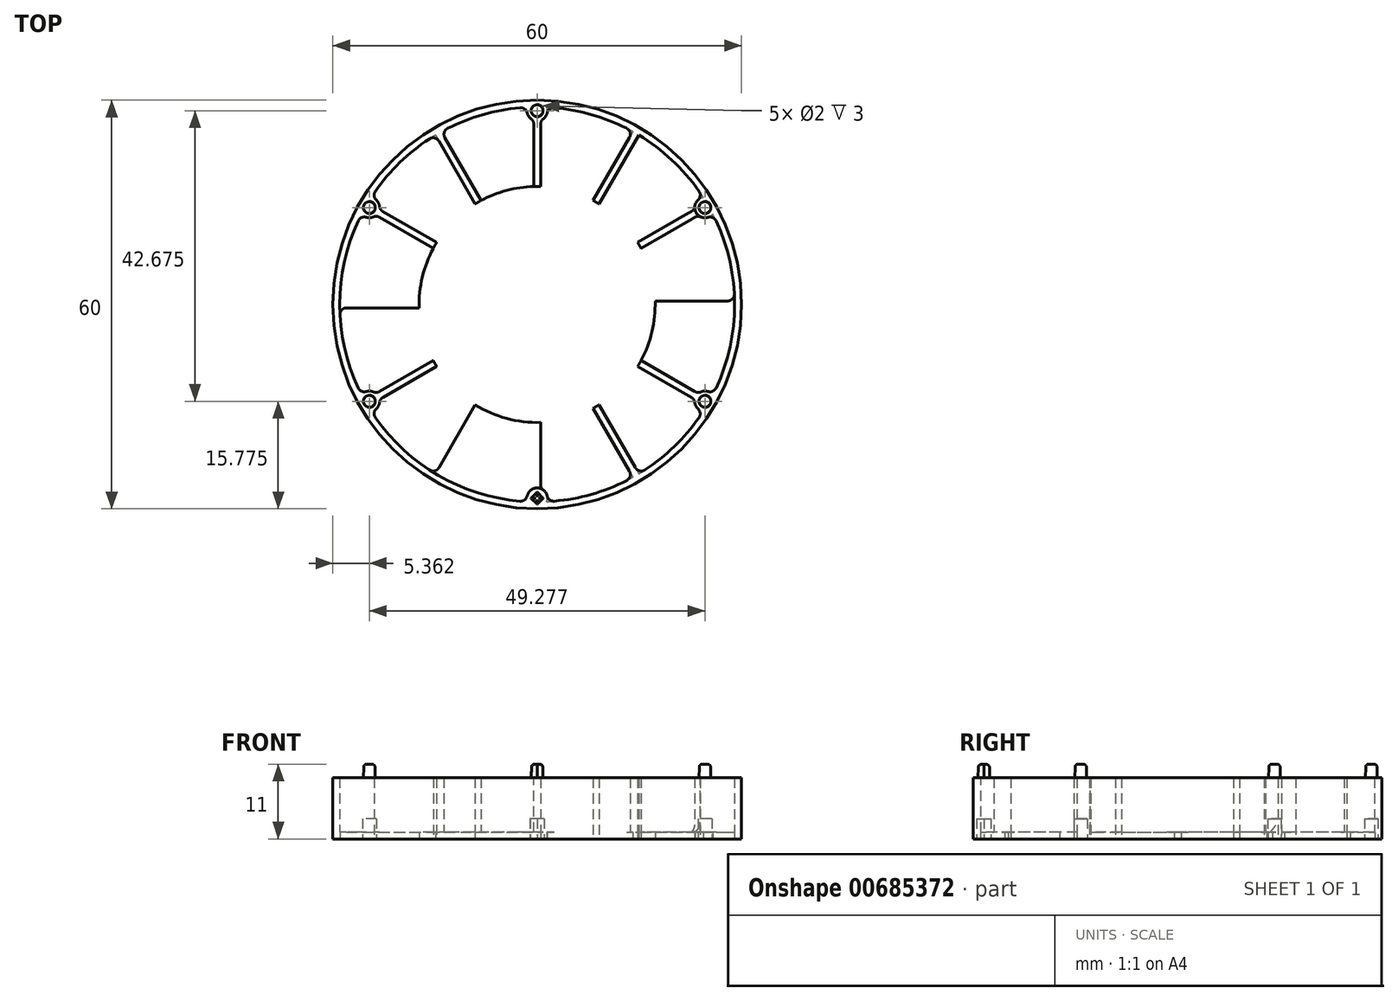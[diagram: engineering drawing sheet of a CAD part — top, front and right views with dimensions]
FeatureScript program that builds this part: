
annotation { "Feature Type Name" : "Feature", "Feature Type Description" : "" }
export const myFeature = defineFeature(function(context is Context, id is Id, definition is map)
    precondition{}
    {
        {
            var Q0;
            Q0=qCreatedBy(makeId("Top.planeOp"),FACE);
            var sketch = newSketch(context, id + "F0", { "sketchPlane" : qUnion([Q0])});
            skCircle(sketch, "E0", {"center": v(0, 0) * mm, "radius": 30 * mm});
            skCircle(sketch, "E1.0", {"center": v(0, 0) * mm, "radius": 29 * mm});
            skLineSegment(sketch, "E2.bottom", {"start": v(14.56, 26.23) * mm, "end": v(15.43, 25.73) * mm});
            skLineSegment(sketch, "E2.top", {"start": v(-15.43, -25.73) * mm, "end": v(-14.56, -26.23) * mm});
            skLineSegment(sketch, "E2.left", {"start": v(14.56, 26.23) * mm, "end": v(-15.43, -25.73) * mm});
            skLineSegment(sketch, "E2.right", {"start": v(15.43, 25.73) * mm, "end": v(-14.56, -26.23) * mm});
            skLineSegment(sketch, "E3.bottom", {"start": v(25.73, 15.43) * mm, "end": v(26.23, 14.56) * mm});
            skLineSegment(sketch, "E3.top", {"start": v(-26.23, -14.56) * mm, "end": v(-25.73, -15.43) * mm});
            skLineSegment(sketch, "E3.left", {"start": v(25.73, 15.43) * mm, "end": v(-26.23, -14.56) * mm});
            skLineSegment(sketch, "E3.right", {"start": v(26.23, 14.56) * mm, "end": v(-25.73, -15.43) * mm});
            skLineSegment(sketch, "E4", {"start": v(-38.35, 0) * mm, "end": v(39.17, 0) * mm, "construction": true});
            skLineSegment(sketch, "E5", {"start": v(0, 42.5) * mm, "end": v(0, -42.47) * mm, "construction": true});
            skLineSegment(sketch, "E6.bottom", {"start": v(-30, 0.5) * mm, "end": v(30, 0.5) * mm});
            skLineSegment(sketch, "E6.top", {"start": v(-30, -0.5) * mm, "end": v(30, -0.5) * mm});
            skLineSegment(sketch, "E6.left", {"start": v(-30, 0.5) * mm, "end": v(-30, -0.5) * mm});
            skLineSegment(sketch, "E6.right", {"start": v(30, 0.5) * mm, "end": v(30, -0.5) * mm});
            skLineSegment(sketch, "E7.bottom", {"start": v(-25.73, 15.43) * mm, "end": v(26.23, -14.56) * mm});
            skLineSegment(sketch, "E7.top", {"start": v(-26.23, 14.56) * mm, "end": v(25.73, -15.43) * mm});
            skLineSegment(sketch, "E7.left", {"start": v(-25.73, 15.43) * mm, "end": v(-26.23, 14.56) * mm});
            skLineSegment(sketch, "E7.right", {"start": v(26.23, -14.56) * mm, "end": v(25.73, -15.43) * mm});
            skLineSegment(sketch, "E8.bottom", {"start": v(-0.5, 30) * mm, "end": v(0.5, 30) * mm});
            skLineSegment(sketch, "E8.top", {"start": v(-0.5, -30) * mm, "end": v(0.5, -30) * mm});
            skLineSegment(sketch, "E8.left", {"start": v(-0.5, 30) * mm, "end": v(-0.5, -30) * mm});
            skLineSegment(sketch, "E8.right", {"start": v(0.5, 30) * mm, "end": v(0.5, -30) * mm});
            skLineSegment(sketch, "E9.bottom", {"start": v(-15.43, 25.73) * mm, "end": v(-14.56, 26.23) * mm});
            skLineSegment(sketch, "E9.top", {"start": v(14.56, -26.23) * mm, "end": v(15.43, -25.73) * mm});
            skLineSegment(sketch, "E9.left", {"start": v(-15.43, 25.73) * mm, "end": v(14.56, -26.23) * mm});
            skLineSegment(sketch, "E9.right", {"start": v(-14.56, 26.23) * mm, "end": v(15.43, -25.73) * mm});
            skCircle(sketch, "E10", {"center": v(0, 0) * mm, "radius": 17.33 * mm});
            skSolve(sketch);
        }
        {
            var Q0;
            Q0=qCreatedBy(makeId("Top.planeOp"),FACE);
            var sketch = newSketch(context, id + "F1", { "sketchPlane" : qUnion([Q0])});
            skCircle(sketch, "E11", {"center": v(0, 0) * mm, "radius": 30 * mm});
            skCircle(sketch, "E12", {"center": v(0, 0) * mm, "radius": 29 * mm});
            skSolve(sketch);
        }
        {
            var Q0;
            Q0=makeQuery(id+"F1.imprint","IMPRINT",FACE,{"disambiguationData":[TD([[makeQuery(id+"F1.imprint","IMPRINT",EDGE,{"derivedFrom":sQuery(id+"F1.wireOp",EDGE,"E11")}),1.0]])]});
            extrude(context, id + "F2", {"entities" : qUnion([Q0]), "depth" : 9 * mm, "offsetDistance" : 25 * mm});
        }
        {
            var Q0;
            {var subQ0=sQuery(id+"F0.wireOp",EDGE,"E7.bottom");var subQ1=sQuery(id+"F0.wireOp",EDGE,"E1.0");var subQ2=makeQuery(id+"F0.imprint","INTERSECT",VERTEX,{"disambiguationData":[OD(0.0)],"derivedFrom":[subQ1,subQ0]});Q0=makeQuery(id+"F0.imprint","IMPRINT",FACE,{"disambiguationData":[TD([[makeQuery(id+"F0.imprint","IMPRINT",EDGE,{"disambiguationData":[TD([[subQ2,-1.0]])],"derivedFrom":subQ1}),1.0]])]});}
            var Q1;
            {var subQ0=sQuery(id+"F0.wireOp",EDGE,"E2.right");var subQ1=sQuery(id+"F0.wireOp",EDGE,"E1.0");var subQ2=makeQuery(id+"F0.imprint","INTERSECT",VERTEX,{"disambiguationData":[OD(0.0)],"derivedFrom":[subQ1,subQ0]});Q1=makeQuery(id+"F0.imprint","IMPRINT",FACE,{"disambiguationData":[TD([[makeQuery(id+"F0.imprint","IMPRINT",EDGE,{"disambiguationData":[TD([[subQ2,-1.0]])],"derivedFrom":subQ1}),1.0]])]});}
            var Q2;
            {var subQ0=sQuery(id+"F0.wireOp",EDGE,"E3.left");var subQ1=sQuery(id+"F0.wireOp",EDGE,"E1.0");var subQ2=makeQuery(id+"F0.imprint","INTERSECT",VERTEX,{"disambiguationData":[OD(1.0)],"derivedFrom":[subQ1,subQ0]});Q2=makeQuery(id+"F0.imprint","IMPRINT",FACE,{"disambiguationData":[TD([[makeQuery(id+"F0.imprint","IMPRINT",EDGE,{"disambiguationData":[TD([[subQ2,-1.0]])],"derivedFrom":subQ1}),1.0]])]});}
            var Q3;
            {var subQ0=sQuery(id+"F0.wireOp",EDGE,"E9.right");var subQ1=sQuery(id+"F0.wireOp",EDGE,"E1.0");var subQ2=makeQuery(id+"F0.imprint","INTERSECT",VERTEX,{"disambiguationData":[OD(0.0)],"derivedFrom":[subQ1,subQ0]});Q3=makeQuery(id+"F0.imprint","IMPRINT",FACE,{"disambiguationData":[TD([[makeQuery(id+"F0.imprint","IMPRINT",EDGE,{"disambiguationData":[TD([[subQ2,-1.0]])],"derivedFrom":subQ1}),1.0]])]});}
            var Q4;
            {var subQ0=sQuery(id+"F0.wireOp",EDGE,"E8.right");var subQ1=sQuery(id+"F0.wireOp",EDGE,"E1.0");var subQ2=makeQuery(id+"F0.imprint","INTERSECT",VERTEX,{"disambiguationData":[OD(0.0)],"derivedFrom":[subQ1,subQ0]});Q4=makeQuery(id+"F0.imprint","IMPRINT",FACE,{"disambiguationData":[TD([[makeQuery(id+"F0.imprint","IMPRINT",EDGE,{"disambiguationData":[TD([[subQ2,-1.0]])],"derivedFrom":subQ1}),1.0]])]});}
            var Q5;
            {var subQ0=sQuery(id+"F0.wireOp",EDGE,"E7.top");var subQ1=sQuery(id+"F0.wireOp",EDGE,"E1.0");var subQ2=makeQuery(id+"F0.imprint","INTERSECT",VERTEX,{"disambiguationData":[OD(1.0)],"derivedFrom":[subQ1,subQ0]});Q5=makeQuery(id+"F0.imprint","IMPRINT",FACE,{"disambiguationData":[TD([[makeQuery(id+"F0.imprint","IMPRINT",EDGE,{"disambiguationData":[TD([[subQ2,-1.0]])],"derivedFrom":subQ1}),1.0]])]});}
            var Q6;
            {var subQ0=sQuery(id+"F0.wireOp",EDGE,"E9.left");var subQ1=sQuery(id+"F0.wireOp",EDGE,"E1.0");var subQ2=makeQuery(id+"F0.imprint","INTERSECT",VERTEX,{"disambiguationData":[OD(1.0)],"derivedFrom":[subQ1,subQ0]});Q6=makeQuery(id+"F0.imprint","IMPRINT",FACE,{"disambiguationData":[TD([[makeQuery(id+"F0.imprint","IMPRINT",EDGE,{"disambiguationData":[TD([[subQ2,-1.0]])],"derivedFrom":subQ1}),1.0]])]});}
            extrude(context, id + "F3", {"entities" : qUnion([Q0, Q1, Q2, Q3, Q4, Q5, Q6]), "operationType" : NewBodyOperationType.ADD, "depth" : 9 * mm, "offsetDistance" : 25 * mm});
        }
        {
            var Q0;
            Q0=makeQuery(id+"F1.imprint","IMPRINT",FACE,{"disambiguationData":[TD([[makeQuery(id+"F1.imprint","IMPRINT",EDGE,{"derivedFrom":sQuery(id+"F1.wireOp",EDGE,"E11")}),1.0]])]});
            var Q1;
            Q1=makeQuery(id+"F1.imprint","IMPRINT",FACE,{"disambiguationData":[TD([[makeQuery(id+"F1.imprint","IMPRINT",EDGE,{"derivedFrom":sQuery(id+"F1.wireOp",EDGE,"E12")}),1.0]])]});
            extrude(context, id + "F4", {"entities" : qUnion([Q0, Q1]), "operationType" : NewBodyOperationType.ADD, "depth" : 1 * mm, "offsetDistance" : 25 * mm});
        }
        {
            var Q0;
            {var subQ0=sQuery(id+"F0.wireOp",EDGE,"E8.right");var subQ1=sQuery(id+"F0.wireOp",EDGE,"E1.0");var subQ2=makeQuery(id+"F0.imprint","INTERSECT",VERTEX,{"disambiguationData":[OD(1.0)],"derivedFrom":[subQ1,subQ0]});Q0=makeQuery(id+"F0.imprint","IMPRINT",FACE,{"disambiguationData":[TD([[makeQuery(id+"F0.imprint","IMPRINT",EDGE,{"disambiguationData":[TD([[subQ2,-1.0]])],"derivedFrom":subQ1}),1.0]])]});}
            var Q1;
            {var subQ0=sQuery(id+"F0.wireOp",EDGE,"E9.right");var subQ1=sQuery(id+"F0.wireOp",EDGE,"E1.0");var subQ2=makeQuery(id+"F0.imprint","INTERSECT",VERTEX,{"disambiguationData":[OD(1.0)],"derivedFrom":[subQ1,subQ0]});Q1=makeQuery(id+"F0.imprint","IMPRINT",FACE,{"disambiguationData":[TD([[makeQuery(id+"F0.imprint","IMPRINT",EDGE,{"disambiguationData":[TD([[subQ2,-1.0]])],"derivedFrom":subQ1}),1.0]])]});}
            var Q2;
            {var subQ0=sQuery(id+"F0.wireOp",EDGE,"E3.right");var subQ1=sQuery(id+"F0.wireOp",EDGE,"E1.0");var subQ2=makeQuery(id+"F0.imprint","INTERSECT",VERTEX,{"disambiguationData":[OD(0.0)],"derivedFrom":[subQ1,subQ0]});Q2=makeQuery(id+"F0.imprint","IMPRINT",FACE,{"disambiguationData":[TD([[makeQuery(id+"F0.imprint","IMPRINT",EDGE,{"disambiguationData":[TD([[subQ2,1.0]])],"derivedFrom":subQ1}),1.0]])]});}
            var Q3;
            {var subQ0=sQuery(id+"F0.wireOp",EDGE,"E3.left");var subQ1=sQuery(id+"F0.wireOp",EDGE,"E1.0");var subQ2=makeQuery(id+"F0.imprint","INTERSECT",VERTEX,{"disambiguationData":[OD(0.0)],"derivedFrom":[subQ1,subQ0]});Q3=makeQuery(id+"F0.imprint","IMPRINT",FACE,{"disambiguationData":[TD([[makeQuery(id+"F0.imprint","IMPRINT",EDGE,{"disambiguationData":[TD([[subQ2,-1.0]])],"derivedFrom":subQ1}),1.0]])]});}
            var Q4;
            {var subQ0=sQuery(id+"F0.wireOp",EDGE,"E2.left");var subQ1=sQuery(id+"F0.wireOp",EDGE,"E1.0");var subQ2=makeQuery(id+"F0.imprint","INTERSECT",VERTEX,{"disambiguationData":[OD(0.0)],"derivedFrom":[subQ1,subQ0]});Q4=makeQuery(id+"F0.imprint","IMPRINT",FACE,{"disambiguationData":[TD([[makeQuery(id+"F0.imprint","IMPRINT",EDGE,{"disambiguationData":[TD([[subQ2,-1.0]])],"derivedFrom":subQ1}),1.0]])]});}
            var Q5;
            {var subQ0=sQuery(id+"F0.wireOp",EDGE,"E9.left");var subQ1=sQuery(id+"F0.wireOp",EDGE,"E1.0");var subQ2=makeQuery(id+"F0.imprint","INTERSECT",VERTEX,{"disambiguationData":[OD(0.0)],"derivedFrom":[subQ1,subQ0]});Q5=makeQuery(id+"F0.imprint","IMPRINT",FACE,{"disambiguationData":[TD([[makeQuery(id+"F0.imprint","IMPRINT",EDGE,{"disambiguationData":[TD([[subQ2,-1.0]])],"derivedFrom":subQ1}),1.0]])]});}
            var Q6;
            {var subQ0=sQuery(id+"F0.wireOp",EDGE,"E6.top");var subQ1=sQuery(id+"F0.wireOp",EDGE,"E1.0");var subQ2=makeQuery(id+"F0.imprint","INTERSECT",VERTEX,{"disambiguationData":[OD(0.0)],"derivedFrom":[subQ1,subQ0]});Q6=makeQuery(id+"F0.imprint","IMPRINT",FACE,{"disambiguationData":[TD([[makeQuery(id+"F0.imprint","IMPRINT",EDGE,{"disambiguationData":[TD([[subQ2,-1.0]])],"derivedFrom":subQ1}),1.0]])]});}
            var Q7;
            {var subQ0=sQuery(id+"F0.wireOp",EDGE,"E3.right");var subQ1=sQuery(id+"F0.wireOp",EDGE,"E1.0");var subQ2=makeQuery(id+"F0.imprint","INTERSECT",VERTEX,{"disambiguationData":[OD(1.0)],"derivedFrom":[subQ1,subQ0]});Q7=makeQuery(id+"F0.imprint","IMPRINT",FACE,{"disambiguationData":[TD([[makeQuery(id+"F0.imprint","IMPRINT",EDGE,{"disambiguationData":[TD([[subQ2,-1.0]])],"derivedFrom":subQ1}),1.0]])]});}
            extrude(context, id + "F5", {"entities" : qUnion([Q0, Q1, Q2, Q3, Q4, Q5, Q6, Q7]), "operationType" : NewBodyOperationType.REMOVE, "depth" : 1 * mm, "offsetDistance" : 25 * mm});
        }
        {
            var Q0;
            Q0=qCreatedBy(makeId("Top.planeOp"),FACE);
            var sketch = newSketch(context, id + "F6", { "sketchPlane" : qUnion([Q0])});
            skCircle(sketch, "E13", {"center": v(0, 0) * mm, "radius": 28.45 * mm});
            skLineSegment(sketch, "E14", {"start": v(0, 28.45) * mm, "end": v(0, -28.45) * mm, "construction": true});
            skLineSegment(sketch, "E15", {"start": v(24.64, 14.22) * mm, "end": v(0, 0) * mm, "construction": true});
            skLineSegment(sketch, "E16", {"start": v(14.23, 24.64) * mm, "end": v(0, 0) * mm, "construction": true});
            skLineSegment(sketch, "E17", {"start": v(0, 0) * mm, "end": v(28.45, 0) * mm, "construction": true});
            skLineSegment(sketch, "E18", {"start": v(0, 0) * mm, "end": v(24.64, -14.22) * mm, "construction": true});
            skLineSegment(sketch, "E19", {"start": v(0, 0) * mm, "end": v(14.23, -24.64) * mm, "construction": true});
            skLineSegment(sketch, "E20", {"start": v(0, 0) * mm, "end": v(-14.23, 24.64) * mm, "construction": true});
            skLineSegment(sketch, "E21", {"start": v(0, 0) * mm, "end": v(-24.64, 14.22) * mm, "construction": true});
            skLineSegment(sketch, "E22", {"start": v(0, 0) * mm, "end": v(-28.45, 0) * mm, "construction": true});
            skLineSegment(sketch, "E23", {"start": v(0, 0) * mm, "end": v(-24.64, -14.23) * mm, "construction": true});
            skLineSegment(sketch, "E24", {"start": v(0, 0) * mm, "end": v(-14.22, -24.64) * mm, "construction": true});
            skCircle(sketch, "E25", {"center": v(0, 28.45) * mm, "radius": 1.5 * mm});
            skCircle(sketch, "E26", {"center": v(24.64, 14.22) * mm, "radius": 1.5 * mm});
            skCircle(sketch, "E27", {"center": v(24.64, -14.22) * mm, "radius": 1.5 * mm});
            skCircle(sketch, "E28", {"center": v(0, -28.45) * mm, "radius": 1.5 * mm});
            skCircle(sketch, "E29", {"center": v(-24.64, -14.23) * mm, "radius": 1.5 * mm});
            skCircle(sketch, "E30", {"center": v(-24.64, 14.22) * mm, "radius": 1.5 * mm});
            skCircle(sketch, "E31", {"center": v(-24.64, 14.22) * mm, "radius": 1 * mm});
            skCircle(sketch, "E32", {"center": v(0, 28.45) * mm, "radius": 1 * mm});
            skCircle(sketch, "E33", {"center": v(24.64, 14.22) * mm, "radius": 1 * mm});
            skCircle(sketch, "E34", {"center": v(24.64, -14.22) * mm, "radius": 1 * mm});
            skCircle(sketch, "E35", {"center": v(-24.64, -14.23) * mm, "radius": 1 * mm});
            skLineSegment(sketch, "E36.bottom", {"start": v(1.06, -28.45) * mm, "end": v(0, -29.51) * mm});
            skLineSegment(sketch, "E36.top", {"start": v(0, -27.39) * mm, "end": v(-1.06, -28.45) * mm});
            skLineSegment(sketch, "E36.left", {"start": v(1.06, -28.45) * mm, "end": v(0, -27.39) * mm});
            skLineSegment(sketch, "E36.right", {"start": v(0, -29.51) * mm, "end": v(-1.06, -28.45) * mm});
            skSolve(sketch);
        }
        {
            var Q0;
            {var subQ0=sQuery(id+"F6.wireOp",EDGE,"E30");var subQ1=sQuery(id+"F6.wireOp",EDGE,"E13");var subQ2=makeQuery(id+"F6.imprint","INTERSECT",VERTEX,{"disambiguationData":[OD(0.0)],"derivedFrom":[subQ1,subQ0]});Q0=makeQuery(id+"F6.imprint","IMPRINT",FACE,{"disambiguationData":[TD([[makeQuery(id+"F6.imprint","IMPRINT",EDGE,{"disambiguationData":[TD([[subQ2,-1.0]])],"derivedFrom":subQ1}),1.0]])]});}
            var Q1;
            {var subQ0=sQuery(id+"F6.wireOp",EDGE,"E30");var subQ1=sQuery(id+"F6.wireOp",EDGE,"E13");var subQ2=makeQuery(id+"F6.imprint","INTERSECT",VERTEX,{"disambiguationData":[OD(0.0)],"derivedFrom":[subQ1,subQ0]});Q1=makeQuery(id+"F6.imprint","IMPRINT",FACE,{"disambiguationData":[TD([[makeQuery(id+"F6.imprint","IMPRINT",EDGE,{"disambiguationData":[TD([[subQ2,-1.0]])],"derivedFrom":subQ1}),-1.0]])]});}
            var Q2;
            {var subQ0=sQuery(id+"F6.wireOp",EDGE,"E25");var subQ1=sQuery(id+"F6.wireOp",EDGE,"E13");var subQ2=makeQuery(id+"F6.imprint","INTERSECT",VERTEX,{"disambiguationData":[OD(0.0)],"derivedFrom":[subQ1,subQ0]});Q2=makeQuery(id+"F6.imprint","IMPRINT",FACE,{"disambiguationData":[TD([[makeQuery(id+"F6.imprint","IMPRINT",EDGE,{"disambiguationData":[TD([[subQ2,-1.0]])],"derivedFrom":subQ1}),1.0]])]});}
            var Q3;
            {var subQ0=sQuery(id+"F6.wireOp",EDGE,"E25");var subQ1=sQuery(id+"F6.wireOp",EDGE,"E13");var subQ2=makeQuery(id+"F6.imprint","INTERSECT",VERTEX,{"disambiguationData":[OD(0.0)],"derivedFrom":[subQ1,subQ0]});Q3=makeQuery(id+"F6.imprint","IMPRINT",FACE,{"disambiguationData":[TD([[makeQuery(id+"F6.imprint","IMPRINT",EDGE,{"disambiguationData":[TD([[subQ2,-1.0]])],"derivedFrom":subQ1}),-1.0]])]});}
            var Q4;
            {var subQ0=sQuery(id+"F6.wireOp",EDGE,"E26");var subQ1=sQuery(id+"F6.wireOp",EDGE,"E13");var subQ2=makeQuery(id+"F6.imprint","INTERSECT",VERTEX,{"disambiguationData":[OD(0.0)],"derivedFrom":[subQ1,subQ0]});Q4=makeQuery(id+"F6.imprint","IMPRINT",FACE,{"disambiguationData":[TD([[makeQuery(id+"F6.imprint","IMPRINT",EDGE,{"disambiguationData":[TD([[subQ2,-1.0]])],"derivedFrom":subQ1}),-1.0]])]});}
            var Q5;
            {var subQ0=sQuery(id+"F6.wireOp",EDGE,"E26");var subQ1=sQuery(id+"F6.wireOp",EDGE,"E13");var subQ2=makeQuery(id+"F6.imprint","INTERSECT",VERTEX,{"disambiguationData":[OD(0.0)],"derivedFrom":[subQ1,subQ0]});Q5=makeQuery(id+"F6.imprint","IMPRINT",FACE,{"disambiguationData":[TD([[makeQuery(id+"F6.imprint","IMPRINT",EDGE,{"disambiguationData":[TD([[subQ2,-1.0]])],"derivedFrom":subQ1}),1.0]])]});}
            var Q6;
            {var subQ0=sQuery(id+"F6.wireOp",EDGE,"E29");var subQ1=sQuery(id+"F6.wireOp",EDGE,"E13");var subQ2=makeQuery(id+"F6.imprint","INTERSECT",VERTEX,{"disambiguationData":[OD(0.0)],"derivedFrom":[subQ1,subQ0]});Q6=makeQuery(id+"F6.imprint","IMPRINT",FACE,{"disambiguationData":[TD([[makeQuery(id+"F6.imprint","IMPRINT",EDGE,{"disambiguationData":[TD([[subQ2,-1.0]])],"derivedFrom":subQ1}),1.0]])]});}
            var Q7;
            {var subQ0=sQuery(id+"F6.wireOp",EDGE,"E29");var subQ1=sQuery(id+"F6.wireOp",EDGE,"E13");var subQ2=makeQuery(id+"F6.imprint","INTERSECT",VERTEX,{"disambiguationData":[OD(0.0)],"derivedFrom":[subQ1,subQ0]});Q7=makeQuery(id+"F6.imprint","IMPRINT",FACE,{"disambiguationData":[TD([[makeQuery(id+"F6.imprint","IMPRINT",EDGE,{"disambiguationData":[TD([[subQ2,-1.0]])],"derivedFrom":subQ1}),-1.0]])]});}
            var Q8;
            {var subQ3=sQuery(id+"F6.wireOp",EDGE,"E13");var subQ5=sQuery(id+"F6.wireOp",EDGE,"E28");var subQ6=makeQuery(id+"F6.imprint","INTERSECT",VERTEX,{"disambiguationData":[OD(0.0)],"derivedFrom":[subQ3,subQ5]});Q8=makeQuery(id+"F6.imprint","IMPRINT",FACE,{"disambiguationData":[TD([[makeQuery(id+"F6.imprint","IMPRINT",EDGE,{"disambiguationData":[TD([[subQ6,-1.0]])],"derivedFrom":subQ3}),1.0]])]});}
            var Q9;
            {var subQ6=sQuery(id+"F6.wireOp",EDGE,"E36.bottom");Q9=makeQuery(id+"F6.imprint","IMPRINT",FACE,{"disambiguationData":[TD([[makeQuery(id+"F6.imprint","IMPRINT",EDGE,{"derivedFrom":subQ6}),1.0]])]});}
            var Q10;
            {var subQ0=sQuery(id+"F6.wireOp",EDGE,"E27");var subQ1=sQuery(id+"F6.wireOp",EDGE,"E13");var subQ2=makeQuery(id+"F6.imprint","INTERSECT",VERTEX,{"disambiguationData":[OD(0.0)],"derivedFrom":[subQ1,subQ0]});Q10=makeQuery(id+"F6.imprint","IMPRINT",FACE,{"disambiguationData":[TD([[makeQuery(id+"F6.imprint","IMPRINT",EDGE,{"disambiguationData":[TD([[subQ2,-1.0]])],"derivedFrom":subQ1}),-1.0]])]});}
            var Q11;
            {var subQ0=sQuery(id+"F6.wireOp",EDGE,"E27");var subQ1=sQuery(id+"F6.wireOp",EDGE,"E13");var subQ2=makeQuery(id+"F6.imprint","INTERSECT",VERTEX,{"disambiguationData":[OD(0.0)],"derivedFrom":[subQ1,subQ0]});Q11=makeQuery(id+"F6.imprint","IMPRINT",FACE,{"disambiguationData":[TD([[makeQuery(id+"F6.imprint","IMPRINT",EDGE,{"disambiguationData":[TD([[subQ2,-1.0]])],"derivedFrom":subQ1}),1.0]])]});}
            var Q12;
            {var subQ0=sQuery(id+"F6.wireOp",EDGE,"E31");var subQ1=sQuery(id+"F6.wireOp",EDGE,"E13");var subQ2=makeQuery(id+"F6.imprint","INTERSECT",VERTEX,{"disambiguationData":[OD(0.0)],"derivedFrom":[subQ1,subQ0]});Q12=makeQuery(id+"F6.imprint","IMPRINT",FACE,{"disambiguationData":[TD([[makeQuery(id+"F6.imprint","IMPRINT",EDGE,{"disambiguationData":[TD([[subQ2,-1.0]])],"derivedFrom":subQ1}),1.0]])]});}
            var Q13;
            {var subQ0=sQuery(id+"F6.wireOp",EDGE,"E31");var subQ1=sQuery(id+"F6.wireOp",EDGE,"E13");var subQ2=makeQuery(id+"F6.imprint","INTERSECT",VERTEX,{"disambiguationData":[OD(0.0)],"derivedFrom":[subQ1,subQ0]});Q13=makeQuery(id+"F6.imprint","IMPRINT",FACE,{"disambiguationData":[TD([[makeQuery(id+"F6.imprint","IMPRINT",EDGE,{"disambiguationData":[TD([[subQ2,-1.0]])],"derivedFrom":subQ1}),-1.0]])]});}
            var Q14;
            {var subQ0=sQuery(id+"F6.wireOp",EDGE,"E32");var subQ1=sQuery(id+"F6.wireOp",EDGE,"E13");var subQ2=makeQuery(id+"F6.imprint","INTERSECT",VERTEX,{"disambiguationData":[OD(0.0)],"derivedFrom":[subQ1,subQ0]});Q14=makeQuery(id+"F6.imprint","IMPRINT",FACE,{"disambiguationData":[TD([[makeQuery(id+"F6.imprint","IMPRINT",EDGE,{"disambiguationData":[TD([[subQ2,-1.0]])],"derivedFrom":subQ1}),-1.0]])]});}
            var Q15;
            {var subQ0=sQuery(id+"F6.wireOp",EDGE,"E32");var subQ1=sQuery(id+"F6.wireOp",EDGE,"E13");var subQ2=makeQuery(id+"F6.imprint","INTERSECT",VERTEX,{"disambiguationData":[OD(0.0)],"derivedFrom":[subQ1,subQ0]});Q15=makeQuery(id+"F6.imprint","IMPRINT",FACE,{"disambiguationData":[TD([[makeQuery(id+"F6.imprint","IMPRINT",EDGE,{"disambiguationData":[TD([[subQ2,-1.0]])],"derivedFrom":subQ1}),1.0]])]});}
            var Q16;
            {var subQ0=sQuery(id+"F6.wireOp",EDGE,"E33");var subQ1=sQuery(id+"F6.wireOp",EDGE,"E13");var subQ2=makeQuery(id+"F6.imprint","INTERSECT",VERTEX,{"disambiguationData":[OD(0.0)],"derivedFrom":[subQ1,subQ0]});Q16=makeQuery(id+"F6.imprint","IMPRINT",FACE,{"disambiguationData":[TD([[makeQuery(id+"F6.imprint","IMPRINT",EDGE,{"disambiguationData":[TD([[subQ2,-1.0]])],"derivedFrom":subQ1}),-1.0]])]});}
            var Q17;
            {var subQ0=sQuery(id+"F6.wireOp",EDGE,"E33");var subQ1=sQuery(id+"F6.wireOp",EDGE,"E13");var subQ2=makeQuery(id+"F6.imprint","INTERSECT",VERTEX,{"disambiguationData":[OD(0.0)],"derivedFrom":[subQ1,subQ0]});Q17=makeQuery(id+"F6.imprint","IMPRINT",FACE,{"disambiguationData":[TD([[makeQuery(id+"F6.imprint","IMPRINT",EDGE,{"disambiguationData":[TD([[subQ2,-1.0]])],"derivedFrom":subQ1}),1.0]])]});}
            var Q18;
            {var subQ0=sQuery(id+"F6.wireOp",EDGE,"E34");var subQ1=sQuery(id+"F6.wireOp",EDGE,"E13");var subQ2=makeQuery(id+"F6.imprint","INTERSECT",VERTEX,{"disambiguationData":[OD(0.0)],"derivedFrom":[subQ1,subQ0]});Q18=makeQuery(id+"F6.imprint","IMPRINT",FACE,{"disambiguationData":[TD([[makeQuery(id+"F6.imprint","IMPRINT",EDGE,{"disambiguationData":[TD([[subQ2,-1.0]])],"derivedFrom":subQ1}),-1.0]])]});}
            var Q19;
            {var subQ0=sQuery(id+"F6.wireOp",EDGE,"E34");var subQ1=sQuery(id+"F6.wireOp",EDGE,"E13");var subQ2=makeQuery(id+"F6.imprint","INTERSECT",VERTEX,{"disambiguationData":[OD(0.0)],"derivedFrom":[subQ1,subQ0]});Q19=makeQuery(id+"F6.imprint","IMPRINT",FACE,{"disambiguationData":[TD([[makeQuery(id+"F6.imprint","IMPRINT",EDGE,{"disambiguationData":[TD([[subQ2,-1.0]])],"derivedFrom":subQ1}),1.0]])]});}
            var Q20;
            {var subQ1=sQuery(id+"F6.wireOp",EDGE,"E36.bottom");Q20=makeQuery(id+"F6.imprint","IMPRINT",FACE,{"disambiguationData":[TD([[makeQuery(id+"F6.imprint","IMPRINT",EDGE,{"derivedFrom":subQ1}),-1.0]])]});}
            var Q21;
            {var subQ0=sQuery(id+"F6.wireOp",EDGE,"E35");var subQ1=sQuery(id+"F6.wireOp",EDGE,"E13");var subQ2=makeQuery(id+"F6.imprint","INTERSECT",VERTEX,{"disambiguationData":[OD(0.0)],"derivedFrom":[subQ1,subQ0]});Q21=makeQuery(id+"F6.imprint","IMPRINT",FACE,{"disambiguationData":[TD([[makeQuery(id+"F6.imprint","IMPRINT",EDGE,{"disambiguationData":[TD([[subQ2,-1.0]])],"derivedFrom":subQ1}),-1.0]])]});}
            var Q22;
            {var subQ0=sQuery(id+"F6.wireOp",EDGE,"E35");var subQ1=sQuery(id+"F6.wireOp",EDGE,"E13");var subQ2=makeQuery(id+"F6.imprint","INTERSECT",VERTEX,{"disambiguationData":[OD(0.0)],"derivedFrom":[subQ1,subQ0]});Q22=makeQuery(id+"F6.imprint","IMPRINT",FACE,{"disambiguationData":[TD([[makeQuery(id+"F6.imprint","IMPRINT",EDGE,{"disambiguationData":[TD([[subQ2,-1.0]])],"derivedFrom":subQ1}),1.0]])]});}
            var Q23;
            {var subQ0=sQuery(id+"F6.wireOp",EDGE,"E36.top");var subQ1=sQuery(id+"F6.wireOp",EDGE,"E13");var subQ2=makeQuery(id+"F6.imprint","INTERSECT",VERTEX,{"derivedFrom":[subQ1,subQ0]});Q23=makeQuery(id+"F6.imprint","IMPRINT",FACE,{"disambiguationData":[TD([[makeQuery(id+"F6.imprint","IMPRINT",EDGE,{"disambiguationData":[TD([[subQ2,-1.0]])],"derivedFrom":subQ1}),1.0]])]});}
            extrude(context, id + "F7", {"entities" : qUnion([Q0, Q1, Q2, Q3, Q4, Q5, Q6, Q7, Q8, Q9, Q10, Q11, Q12, Q13, Q14, Q15, Q16, Q17, Q18, Q19, Q20, Q21, Q22, Q23]), "operationType" : NewBodyOperationType.ADD, "depth" : 9 * mm, "offsetDistance" : 25 * mm});
        }
        {
            var Q0;
            {var subQ0=sQuery(id+"F0.wireOp",EDGE,"E8.right");var subQ1=sQuery(id+"F0.wireOp",EDGE,"E1.0");Q0=makeQuery(id+"F3.opExtrude","SWEPT_EDGE",EDGE,{"disambiguationData":[OSD([subQ1,subQ0]),TDD([makeQuery(id+"F0.imprint","INTERSECT",VERTEX,{"disambiguationData":[OD(1.0)],"derivedFrom":[subQ1,subQ0]})])]});}
            var Q1;
            {var subQ0=sQuery(id+"F0.wireOp",EDGE,"E2.left");var subQ1=sQuery(id+"F0.wireOp",EDGE,"E1.0");Q1=makeQuery(id+"F3.opExtrude","SWEPT_EDGE",EDGE,{"disambiguationData":[OSD([subQ1,subQ0]),TDD([makeQuery(id+"F0.imprint","INTERSECT",VERTEX,{"disambiguationData":[OD(1.0)],"derivedFrom":[subQ1,subQ0]})])]});}
            var Q2;
            {var subQ0=sQuery(id+"F0.wireOp",EDGE,"E3.left");var subQ1=sQuery(id+"F0.wireOp",EDGE,"E1.0");Q2=makeQuery(id+"F3.opExtrude","SWEPT_EDGE",EDGE,{"disambiguationData":[OSD([subQ1,subQ0]),TDD([makeQuery(id+"F0.imprint","INTERSECT",VERTEX,{"disambiguationData":[OD(1.0)],"derivedFrom":[subQ1,subQ0]})])]});}
            var Q3;
            {var subQ0=sQuery(id+"F0.wireOp",EDGE,"E6.bottom");var subQ1=sQuery(id+"F0.wireOp",EDGE,"E1.0");Q3=makeQuery(id+"F3.opExtrude","SWEPT_EDGE",EDGE,{"disambiguationData":[OSD([subQ1,subQ0]),TDD([makeQuery(id+"F0.imprint","INTERSECT",VERTEX,{"disambiguationData":[OD(1.0)],"derivedFrom":[subQ1,subQ0]})])]});}
            var Q4;
            {var subQ0=sQuery(id+"F0.wireOp",EDGE,"E9.right");var subQ1=sQuery(id+"F0.wireOp",EDGE,"E1.0");Q4=makeQuery(id+"F3.opExtrude","SWEPT_EDGE",EDGE,{"disambiguationData":[OSD([subQ1,subQ0]),TDD([makeQuery(id+"F0.imprint","INTERSECT",VERTEX,{"disambiguationData":[OD(1.0)],"derivedFrom":[subQ1,subQ0]})])]});}
            var Q5;
            {var subQ0=sQuery(id+"F0.wireOp",EDGE,"E7.bottom");var subQ1=sQuery(id+"F0.wireOp",EDGE,"E1.0");Q5=makeQuery(id+"F3.opExtrude","SWEPT_EDGE",EDGE,{"disambiguationData":[OSD([subQ1,subQ0]),TDD([makeQuery(id+"F0.imprint","INTERSECT",VERTEX,{"disambiguationData":[OD(1.0)],"derivedFrom":[subQ1,subQ0]})])]});}
            var Q6;
            {var subQ0=sQuery(id+"F0.wireOp",EDGE,"E8.left");var subQ1=sQuery(id+"F0.wireOp",EDGE,"E1.0");Q6=makeQuery(id+"F3.opExtrude","SWEPT_EDGE",EDGE,{"disambiguationData":[OSD([subQ1,subQ0]),TDD([makeQuery(id+"F0.imprint","INTERSECT",VERTEX,{"disambiguationData":[OD(0.0)],"derivedFrom":[subQ1,subQ0]})])]});}
            var Q7;
            {var subQ0=sQuery(id+"F0.wireOp",EDGE,"E2.left");var subQ1=sQuery(id+"F0.wireOp",EDGE,"E1.0");Q7=makeQuery(id+"F3.opExtrude","SWEPT_EDGE",EDGE,{"disambiguationData":[OSD([subQ1,subQ0]),TDD([makeQuery(id+"F0.imprint","INTERSECT",VERTEX,{"disambiguationData":[OD(0.0)],"derivedFrom":[subQ1,subQ0]})])]});}
            var Q8;
            {var subQ0=sQuery(id+"F0.wireOp",EDGE,"E3.left");var subQ1=sQuery(id+"F0.wireOp",EDGE,"E1.0");Q8=makeQuery(id+"F3.opExtrude","SWEPT_EDGE",EDGE,{"disambiguationData":[OSD([subQ1,subQ0]),TDD([makeQuery(id+"F0.imprint","INTERSECT",VERTEX,{"disambiguationData":[OD(0.0)],"derivedFrom":[subQ1,subQ0]})])]});}
            var Q9;
            {var subQ0=sQuery(id+"F0.wireOp",EDGE,"E6.top");var subQ1=sQuery(id+"F0.wireOp",EDGE,"E1.0");Q9=makeQuery(id+"F3.opExtrude","SWEPT_EDGE",EDGE,{"disambiguationData":[OSD([subQ1,subQ0]),TDD([makeQuery(id+"F0.imprint","INTERSECT",VERTEX,{"disambiguationData":[OD(1.0)],"derivedFrom":[subQ1,subQ0]})])]});}
            var Q10;
            {var subQ0=sQuery(id+"F0.wireOp",EDGE,"E7.top");var subQ1=sQuery(id+"F0.wireOp",EDGE,"E1.0");Q10=makeQuery(id+"F3.opExtrude","SWEPT_EDGE",EDGE,{"disambiguationData":[OSD([subQ1,subQ0]),TDD([makeQuery(id+"F0.imprint","INTERSECT",VERTEX,{"disambiguationData":[OD(0.0)],"derivedFrom":[subQ1,subQ0]})])]});}
            var Q11;
            {var subQ0=sQuery(id+"F0.wireOp",EDGE,"E6.top");var subQ1=sQuery(id+"F0.wireOp",EDGE,"E1.0");Q11=makeQuery(id+"F3.opExtrude","SWEPT_EDGE",EDGE,{"disambiguationData":[OSD([subQ1,subQ0]),TDD([makeQuery(id+"F0.imprint","INTERSECT",VERTEX,{"disambiguationData":[OD(0.0)],"derivedFrom":[subQ1,subQ0]})])]});}
            var Q12;
            {var subQ0=sQuery(id+"F0.wireOp",EDGE,"E9.left");var subQ1=sQuery(id+"F0.wireOp",EDGE,"E1.0");Q12=makeQuery(id+"F3.opExtrude","SWEPT_EDGE",EDGE,{"disambiguationData":[OSD([subQ1,subQ0]),TDD([makeQuery(id+"F0.imprint","INTERSECT",VERTEX,{"disambiguationData":[OD(0.0)],"derivedFrom":[subQ1,subQ0]})])]});}
            var Q13;
            {var subQ0=sQuery(id+"F0.wireOp",EDGE,"E8.right");var subQ1=sQuery(id+"F0.wireOp",EDGE,"E1.0");Q13=makeQuery(id+"F3.opExtrude","SWEPT_EDGE",EDGE,{"disambiguationData":[OSD([subQ1,subQ0]),TDD([makeQuery(id+"F0.imprint","INTERSECT",VERTEX,{"disambiguationData":[OD(0.0)],"derivedFrom":[subQ1,subQ0]})])]});}
            var Q14;
            {var subQ0=sQuery(id+"F0.wireOp",EDGE,"E7.bottom");var subQ1=sQuery(id+"F0.wireOp",EDGE,"E1.0");Q14=makeQuery(id+"F3.opExtrude","SWEPT_EDGE",EDGE,{"disambiguationData":[OSD([subQ1,subQ0]),TDD([makeQuery(id+"F0.imprint","INTERSECT",VERTEX,{"disambiguationData":[OD(0.0)],"derivedFrom":[subQ1,subQ0]})])]});}
            var Q15;
            {var subQ0=sQuery(id+"F0.wireOp",EDGE,"E9.right");var subQ1=sQuery(id+"F0.wireOp",EDGE,"E1.0");Q15=makeQuery(id+"F3.opExtrude","SWEPT_EDGE",EDGE,{"disambiguationData":[OSD([subQ1,subQ0]),TDD([makeQuery(id+"F0.imprint","INTERSECT",VERTEX,{"disambiguationData":[OD(0.0)],"derivedFrom":[subQ1,subQ0]})])]});}
            var Q16;
            {var subQ0=sQuery(id+"F0.wireOp",EDGE,"E3.right");var subQ1=sQuery(id+"F0.wireOp",EDGE,"E1.0");Q16=makeQuery(id+"F3.opExtrude","SWEPT_EDGE",EDGE,{"disambiguationData":[OSD([subQ1,subQ0]),TDD([makeQuery(id+"F0.imprint","INTERSECT",VERTEX,{"disambiguationData":[OD(1.0)],"derivedFrom":[subQ1,subQ0]})])]});}
            var Q17;
            {var subQ0=sQuery(id+"F0.wireOp",EDGE,"E2.right");var subQ1=sQuery(id+"F0.wireOp",EDGE,"E1.0");Q17=makeQuery(id+"F3.opExtrude","SWEPT_EDGE",EDGE,{"disambiguationData":[OSD([subQ1,subQ0]),TDD([makeQuery(id+"F0.imprint","INTERSECT",VERTEX,{"disambiguationData":[OD(1.0)],"derivedFrom":[subQ1,subQ0]})])]});}
            var Q18;
            {var subQ0=sQuery(id+"F0.wireOp",EDGE,"E3.right");var subQ1=sQuery(id+"F0.wireOp",EDGE,"E1.0");Q18=makeQuery(id+"F3.opExtrude","SWEPT_EDGE",EDGE,{"disambiguationData":[OSD([subQ1,subQ0]),TDD([makeQuery(id+"F0.imprint","INTERSECT",VERTEX,{"disambiguationData":[OD(0.0)],"derivedFrom":[subQ1,subQ0]})])]});}
            var Q19;
            {var subQ0=sQuery(id+"F0.wireOp",EDGE,"E2.right");var subQ1=sQuery(id+"F0.wireOp",EDGE,"E1.0");Q19=makeQuery(id+"F3.opExtrude","SWEPT_EDGE",EDGE,{"disambiguationData":[OSD([subQ1,subQ0]),TDD([makeQuery(id+"F0.imprint","INTERSECT",VERTEX,{"disambiguationData":[OD(0.0)],"derivedFrom":[subQ1,subQ0]})])]});}
            var Q20;
            {var subQ0=sQuery(id+"F0.wireOp",EDGE,"E8.left");var subQ1=sQuery(id+"F0.wireOp",EDGE,"E1.0");Q20=makeQuery(id+"F3.opExtrude","SWEPT_EDGE",EDGE,{"disambiguationData":[OSD([subQ1,subQ0]),TDD([makeQuery(id+"F0.imprint","INTERSECT",VERTEX,{"disambiguationData":[OD(1.0)],"derivedFrom":[subQ1,subQ0]})])]});}
            var Q21;
            {var subQ0=sQuery(id+"F0.wireOp",EDGE,"E9.left");var subQ1=sQuery(id+"F0.wireOp",EDGE,"E1.0");Q21=makeQuery(id+"F3.opExtrude","SWEPT_EDGE",EDGE,{"disambiguationData":[OSD([subQ1,subQ0]),TDD([makeQuery(id+"F0.imprint","INTERSECT",VERTEX,{"disambiguationData":[OD(1.0)],"derivedFrom":[subQ1,subQ0]})])]});}
            var Q22;
            {var subQ0=sQuery(id+"F0.wireOp",EDGE,"E7.top");var subQ1=sQuery(id+"F0.wireOp",EDGE,"E1.0");Q22=makeQuery(id+"F3.opExtrude","SWEPT_EDGE",EDGE,{"disambiguationData":[OSD([subQ1,subQ0]),TDD([makeQuery(id+"F0.imprint","INTERSECT",VERTEX,{"disambiguationData":[OD(1.0)],"derivedFrom":[subQ1,subQ0]})])]});}
            var Q23;
            {var subQ0=sQuery(id+"F0.wireOp",EDGE,"E6.bottom");var subQ1=sQuery(id+"F0.wireOp",EDGE,"E1.0");Q23=makeQuery(id+"F3.opExtrude","SWEPT_EDGE",EDGE,{"disambiguationData":[OSD([subQ1,subQ0]),TDD([makeQuery(id+"F0.imprint","INTERSECT",VERTEX,{"disambiguationData":[OD(0.0)],"derivedFrom":[subQ1,subQ0]})])]});}
            var Q24;
            {var subQ23=sQuery(id+"F0.wireOp",EDGE,"E8.left");var subQ24=sQuery(id+"F1.wireOp",EDGE,"E12");Q24=makeQuery(id+"F7.boolean.opBoolean","INTERSECT",EDGE,{"derivedFrom":[makeQuery(id+"F3.boolean.opBoolean","SPLIT",FACE,{"disambiguationData":[TD([makeQuery(id+"F3.opExtrude","SWEPT_FACE",FACE,{"disambiguationData":[OSD([subQ23])]})])],"derivedFrom":makeQuery(id+"F2.opExtrude","SWEPT_FACE",FACE,{"disambiguationData":[OSD([subQ24])]})}),makeQuery(id+"F7.opExtrude","SWEPT_FACE",FACE,{"disambiguationData":[OSD([sQuery(id+"F6.wireOp",EDGE,"E25")])]})]});}
            var Q25;
            {var subQ24=sQuery(id+"F1.wireOp",EDGE,"E12");var subQ34=sQuery(id+"F0.wireOp",EDGE,"E2.right");Q25=makeQuery(id+"F7.boolean.opBoolean","INTERSECT",EDGE,{"disambiguationData":[OD(1.0)],"derivedFrom":[makeQuery(id+"F3.boolean.opBoolean","SPLIT",FACE,{"disambiguationData":[TD([makeQuery(id+"F3.opExtrude","SWEPT_FACE",FACE,{"disambiguationData":[OSD([subQ34])]})])],"derivedFrom":makeQuery(id+"F2.opExtrude","SWEPT_FACE",FACE,{"disambiguationData":[OSD([subQ24])]})}),makeQuery(id+"F7.opExtrude","SWEPT_FACE",FACE,{"disambiguationData":[OSD([sQuery(id+"F6.wireOp",EDGE,"E26")])]})]});}
            var Q26;
            {var subQ24=sQuery(id+"F1.wireOp",EDGE,"E12");var subQ37=sQuery(id+"F0.wireOp",EDGE,"E3.left");Q26=makeQuery(id+"F7.boolean.opBoolean","INTERSECT",EDGE,{"derivedFrom":[makeQuery(id+"F3.boolean.opBoolean","SPLIT",FACE,{"disambiguationData":[TD([makeQuery(id+"F3.opExtrude","SWEPT_FACE",FACE,{"disambiguationData":[OSD([subQ37])]})])],"derivedFrom":makeQuery(id+"F2.opExtrude","SWEPT_FACE",FACE,{"disambiguationData":[OSD([subQ24])]})}),makeQuery(id+"F7.opExtrude","SWEPT_FACE",FACE,{"disambiguationData":[OSD([sQuery(id+"F6.wireOp",EDGE,"E30")])]})]});}
            var Q27;
            {var subQ3=sQuery(id+"F0.wireOp",EDGE,"E7.top");var subQ6=sQuery(id+"F0.wireOp",EDGE,"E1.0");var subQ27=makeQuery(id+"F0.imprint","INTERSECT",VERTEX,{"disambiguationData":[OD(1.0)],"derivedFrom":[subQ6,subQ3]});var subQ29=makeQuery(id+"F0.imprint","IMPRINT",EDGE,{"disambiguationData":[TD([[subQ27,1.0]])],"derivedFrom":subQ3});var subQ30=sQuery(id+"F1.wireOp",EDGE,"E12");Q27=makeQuery(id+"F7.boolean.opBoolean","INTERSECT",EDGE,{"derivedFrom":[makeQuery(id+"F3.boolean.opBoolean","SPLIT",FACE,{"disambiguationData":[TD([makeQuery(id+"F3.opExtrude","SWEPT_FACE",FACE,{"disambiguationData":[OSD([subQ3]),TDD([subQ29])]})])],"derivedFrom":makeQuery(id+"F2.opExtrude","SWEPT_FACE",FACE,{"disambiguationData":[OSD([subQ30])]})}),makeQuery(id+"F7.opExtrude","SWEPT_FACE",FACE,{"disambiguationData":[OSD([sQuery(id+"F6.wireOp",EDGE,"E27")])]})]});}
            var Q28;
            {var subQ24=sQuery(id+"F1.wireOp",EDGE,"E12");var subQ36=sQuery(id+"F0.wireOp",EDGE,"E3.right");Q28=makeQuery(id+"F7.boolean.opBoolean","INTERSECT",EDGE,{"disambiguationData":[OD(0.0)],"derivedFrom":[makeQuery(id+"F3.boolean.opBoolean","SPLIT",FACE,{"disambiguationData":[TD([makeQuery(id+"F3.opExtrude","SWEPT_FACE",FACE,{"disambiguationData":[OSD([subQ36])]})])],"derivedFrom":makeQuery(id+"F2.opExtrude","SWEPT_FACE",FACE,{"disambiguationData":[OSD([subQ24])]})}),makeQuery(id+"F7.opExtrude","SWEPT_FACE",FACE,{"disambiguationData":[OSD([sQuery(id+"F6.wireOp",EDGE,"E28")])]})]});}
            var Q29;
            {var subQ24=sQuery(id+"F1.wireOp",EDGE,"E12");var subQ37=sQuery(id+"F0.wireOp",EDGE,"E3.left");Q29=makeQuery(id+"F7.boolean.opBoolean","INTERSECT",EDGE,{"derivedFrom":[makeQuery(id+"F3.boolean.opBoolean","SPLIT",FACE,{"disambiguationData":[TD([makeQuery(id+"F3.opExtrude","SWEPT_FACE",FACE,{"disambiguationData":[OSD([subQ37])]})])],"derivedFrom":makeQuery(id+"F2.opExtrude","SWEPT_FACE",FACE,{"disambiguationData":[OSD([subQ24])]})}),makeQuery(id+"F7.opExtrude","SWEPT_FACE",FACE,{"disambiguationData":[OSD([sQuery(id+"F6.wireOp",EDGE,"E29")])]})]});}
            var Q30;
            {var subQ24=sQuery(id+"F1.wireOp",EDGE,"E12");var subQ36=sQuery(id+"F0.wireOp",EDGE,"E3.right");Q30=makeQuery(id+"F7.boolean.opBoolean","INTERSECT",EDGE,{"derivedFrom":[makeQuery(id+"F3.boolean.opBoolean","SPLIT",FACE,{"disambiguationData":[TD([makeQuery(id+"F3.opExtrude","SWEPT_FACE",FACE,{"disambiguationData":[OSD([subQ36])]})])],"derivedFrom":makeQuery(id+"F2.opExtrude","SWEPT_FACE",FACE,{"disambiguationData":[OSD([subQ24])]})}),makeQuery(id+"F7.opExtrude","SWEPT_FACE",FACE,{"disambiguationData":[OSD([sQuery(id+"F6.wireOp",EDGE,"E29")])]})]});}
            var Q31;
            {var subQ1=sQuery(id+"F0.wireOp",EDGE,"E7.bottom");var subQ6=sQuery(id+"F0.wireOp",EDGE,"E1.0");var subQ9=makeQuery(id+"F0.imprint","INTERSECT",VERTEX,{"disambiguationData":[OD(0.0)],"derivedFrom":[subQ6,subQ1]});var subQ10=makeQuery(id+"F0.imprint","IMPRINT",EDGE,{"disambiguationData":[TD([[subQ9,-1.0]])],"derivedFrom":subQ1});var subQ24=sQuery(id+"F1.wireOp",EDGE,"E12");Q31=makeQuery(id+"F7.boolean.opBoolean","INTERSECT",EDGE,{"derivedFrom":[makeQuery(id+"F3.boolean.opBoolean","SPLIT",FACE,{"disambiguationData":[TD([makeQuery(id+"F3.opExtrude","SWEPT_FACE",FACE,{"disambiguationData":[OSD([subQ1]),TDD([subQ10])]})])],"derivedFrom":makeQuery(id+"F2.opExtrude","SWEPT_FACE",FACE,{"disambiguationData":[OSD([subQ24])]})}),makeQuery(id+"F7.opExtrude","SWEPT_FACE",FACE,{"disambiguationData":[OSD([sQuery(id+"F6.wireOp",EDGE,"E30")])]})]});}
            var Q32;
            {var subQ24=sQuery(id+"F1.wireOp",EDGE,"E12");var subQ34=sQuery(id+"F0.wireOp",EDGE,"E2.right");Q32=makeQuery(id+"F7.boolean.opBoolean","INTERSECT",EDGE,{"derivedFrom":[makeQuery(id+"F3.boolean.opBoolean","SPLIT",FACE,{"disambiguationData":[TD([makeQuery(id+"F3.opExtrude","SWEPT_FACE",FACE,{"disambiguationData":[OSD([subQ34])]})])],"derivedFrom":makeQuery(id+"F2.opExtrude","SWEPT_FACE",FACE,{"disambiguationData":[OSD([subQ24])]})}),makeQuery(id+"F7.opExtrude","SWEPT_FACE",FACE,{"disambiguationData":[OSD([sQuery(id+"F6.wireOp",EDGE,"E27")])]})]});}
            var Q33;
            {var subQ24=sQuery(id+"F1.wireOp",EDGE,"E12");var subQ35=sQuery(id+"F0.wireOp",EDGE,"E2.left");Q33=makeQuery(id+"F7.boolean.opBoolean","INTERSECT",EDGE,{"derivedFrom":[makeQuery(id+"F3.boolean.opBoolean","SPLIT",FACE,{"disambiguationData":[TD([makeQuery(id+"F3.opExtrude","SWEPT_FACE",FACE,{"disambiguationData":[OSD([subQ35])]})])],"derivedFrom":makeQuery(id+"F2.opExtrude","SWEPT_FACE",FACE,{"disambiguationData":[OSD([subQ24])]})}),makeQuery(id+"F7.opExtrude","SWEPT_FACE",FACE,{"disambiguationData":[OSD([sQuery(id+"F6.wireOp",EDGE,"E25")])]})]});}
            var Q34;
            {var subQ24=sQuery(id+"F1.wireOp",EDGE,"E12");var subQ36=sQuery(id+"F0.wireOp",EDGE,"E3.right");Q34=makeQuery(id+"F7.boolean.opBoolean","INTERSECT",EDGE,{"disambiguationData":[OD(1.0)],"derivedFrom":[makeQuery(id+"F3.boolean.opBoolean","SPLIT",FACE,{"disambiguationData":[TD([makeQuery(id+"F3.opExtrude","SWEPT_FACE",FACE,{"disambiguationData":[OSD([subQ36])]})])],"derivedFrom":makeQuery(id+"F2.opExtrude","SWEPT_FACE",FACE,{"disambiguationData":[OSD([subQ24])]})}),makeQuery(id+"F7.opExtrude","SWEPT_FACE",FACE,{"disambiguationData":[OSD([sQuery(id+"F6.wireOp",EDGE,"E28")])]})]});}
            var Q35;
            {var subQ0=sQuery(id+"F0.wireOp",EDGE,"E3.right");Q35=makeQuery(id+"F7.boolean.opBoolean","INTERSECT",EDGE,{"derivedFrom":[makeQuery(id+"F5.boolean.opBoolean","COPY",FACE,{"derivedFrom":makeQuery(id+"F5.opExtrude","SWEPT_FACE",FACE,{"disambiguationData":[OSD([subQ0]),TDD([makeQuery(id+"F0.imprint","IMPRINT",EDGE,{"disambiguationData":[TD([[makeQuery(id+"F0.imprint","INTERSECT",VERTEX,{"disambiguationData":[OD(0.0)],"derivedFrom":[sQuery(id+"F0.wireOp",EDGE,"E1.0"),subQ0]}),-1.0]])],"derivedFrom":subQ0})])]})}),makeQuery(id+"F7.opExtrude","SWEPT_FACE",FACE,{"disambiguationData":[OSD([sQuery(id+"F6.wireOp",EDGE,"E26")])]})]});}
            var Q36;
            {var subQ0=sQuery(id+"F0.wireOp",EDGE,"E3.left");Q36=makeQuery(id+"F7.boolean.opBoolean","INTERSECT",EDGE,{"derivedFrom":[makeQuery(id+"F5.boolean.opBoolean","COPY",FACE,{"derivedFrom":makeQuery(id+"F5.opExtrude","SWEPT_FACE",FACE,{"disambiguationData":[OSD([subQ0]),TDD([makeQuery(id+"F0.imprint","IMPRINT",EDGE,{"disambiguationData":[TD([[makeQuery(id+"F0.imprint","INTERSECT",VERTEX,{"disambiguationData":[OD(0.0)],"derivedFrom":[sQuery(id+"F0.wireOp",EDGE,"E1.0"),subQ0]}),-1.0]])],"derivedFrom":subQ0})])]})}),makeQuery(id+"F7.opExtrude","SWEPT_FACE",FACE,{"disambiguationData":[OSD([sQuery(id+"F6.wireOp",EDGE,"E26")])]})]});}
            var Q37;
            Q37=makeQuery(id+"F7.boolean.opBoolean","INTERSECT",EDGE,{"derivedFrom":[makeQuery(id+"F4.opExtrude","CAP_FACE",FACE,{"disambiguationData":[OSD([sQuery(id+"F1.wireOp",EDGE,"E11")])],"isStart":false}),makeQuery(id+"F7.opExtrude","SWEPT_FACE",FACE,{"disambiguationData":[OSD([sQuery(id+"F6.wireOp",EDGE,"E26")])]})]});
            var Q38;
            {var subQ0=sQuery(id+"F0.wireOp",EDGE,"E3.left");var subQ1=sQuery(id+"F0.wireOp",EDGE,"E1.0");var subQ2=sQuery(id+"F0.wireOp",EDGE,"E2.right");var subQ3=sQuery(id+"F0.wireOp",EDGE,"E3.right");var subQ27=sQuery(id+"F1.wireOp",EDGE,"E12");Q38=makeQuery(id+"F7.boolean.opBoolean","INTERSECT",EDGE,{"disambiguationData":[OD(0.0)],"derivedFrom":[makeQuery(id+"F5.boolean.opBoolean","MERGE",FACE,{"derivedFrom":[makeQuery(id+"F3.boolean.opBoolean","SPLIT",FACE,{"disambiguationData":[TD([makeQuery(id+"F3.opExtrude","SWEPT_FACE",FACE,{"disambiguationData":[OSD([subQ2])]})])],"derivedFrom":makeQuery(id+"F2.opExtrude","SWEPT_FACE",FACE,{"disambiguationData":[OSD([subQ27])]})}),makeQuery(id+"F5.opExtrude","SWEPT_FACE",FACE,{"disambiguationData":[OSD([subQ1]),TDD([makeQuery(id+"F0.imprint","IMPRINT",EDGE,{"disambiguationData":[TD([[makeQuery(id+"F0.imprint","INTERSECT",VERTEX,{"disambiguationData":[OD(0.0)],"derivedFrom":[subQ1,subQ3]}),1.0]])],"derivedFrom":subQ1})])]}),makeQuery(id+"F5.opExtrude","SWEPT_FACE",FACE,{"disambiguationData":[OSD([subQ1]),TDD([makeQuery(id+"F0.imprint","IMPRINT",EDGE,{"disambiguationData":[TD([[makeQuery(id+"F0.imprint","INTERSECT",VERTEX,{"disambiguationData":[OD(0.0)],"derivedFrom":[subQ1,subQ0]}),-1.0]])],"derivedFrom":subQ1})])]})]}),makeQuery(id+"F7.opExtrude","SWEPT_FACE",FACE,{"disambiguationData":[OSD([sQuery(id+"F6.wireOp",EDGE,"E26")])]})]});}
            var Q39;
            {var subQ0=sQuery(id+"F0.wireOp",EDGE,"E8.right");Q39=makeQuery(id+"F7.boolean.opBoolean","INTERSECT",EDGE,{"derivedFrom":[makeQuery(id+"F5.boolean.opBoolean","COPY",FACE,{"derivedFrom":makeQuery(id+"F5.opExtrude","SWEPT_FACE",FACE,{"disambiguationData":[OSD([subQ0]),TDD([makeQuery(id+"F0.imprint","IMPRINT",EDGE,{"disambiguationData":[TD([[makeQuery(id+"F0.imprint","INTERSECT",VERTEX,{"disambiguationData":[OD(1.0)],"derivedFrom":[sQuery(id+"F0.wireOp",EDGE,"E1.0"),subQ0]}),1.0]])],"derivedFrom":subQ0})])]})}),makeQuery(id+"F7.opExtrude","SWEPT_FACE",FACE,{"disambiguationData":[OSD([sQuery(id+"F6.wireOp",EDGE,"E28")])]})]});}
            var Q40;
            {var subQ0=sQuery(id+"F0.wireOp",EDGE,"E7.bottom");Q40=makeQuery(id+"F7.boolean.opBoolean","INTERSECT",EDGE,{"derivedFrom":[makeQuery(id+"F3.opExtrude","SWEPT_FACE",FACE,{"disambiguationData":[OSD([subQ0]),TDD([makeQuery(id+"F0.imprint","IMPRINT",EDGE,{"disambiguationData":[TD([[makeQuery(id+"F0.imprint","INTERSECT",VERTEX,{"disambiguationData":[OD(1.0)],"derivedFrom":[sQuery(id+"F0.wireOp",EDGE,"E1.0"),subQ0]}),1.0]])],"derivedFrom":subQ0})])]}),makeQuery(id+"F7.opExtrude","SWEPT_FACE",FACE,{"disambiguationData":[OSD([sQuery(id+"F6.wireOp",EDGE,"E27")])]})]});}
            var Q41;
            {var subQ0=sQuery(id+"F0.wireOp",EDGE,"E7.top");Q41=makeQuery(id+"F7.boolean.opBoolean","INTERSECT",EDGE,{"derivedFrom":[makeQuery(id+"F5.boolean.opBoolean","MERGE",FACE,{"derivedFrom":[makeQuery(id+"F3.opExtrude","SWEPT_FACE",FACE,{"disambiguationData":[OSD([subQ0]),TDD([makeQuery(id+"F0.imprint","IMPRINT",EDGE,{"disambiguationData":[TD([[makeQuery(id+"F0.imprint","INTERSECT",VERTEX,{"disambiguationData":[OD(1.0)],"derivedFrom":[sQuery(id+"F0.wireOp",EDGE,"E1.0"),subQ0]}),1.0]])],"derivedFrom":subQ0})])]}),makeQuery(id+"F5.opExtrude","SWEPT_FACE",FACE,{"disambiguationData":[OSD([subQ0])]})]}),makeQuery(id+"F7.opExtrude","SWEPT_FACE",FACE,{"disambiguationData":[OSD([sQuery(id+"F6.wireOp",EDGE,"E27")])]})]});}
            var Q42;
            {var subQ0=sQuery(id+"F0.wireOp",EDGE,"E3.left");Q42=makeQuery(id+"F7.boolean.opBoolean","INTERSECT",EDGE,{"derivedFrom":[makeQuery(id+"F5.boolean.opBoolean","MERGE",FACE,{"derivedFrom":[makeQuery(id+"F3.opExtrude","SWEPT_FACE",FACE,{"disambiguationData":[OSD([subQ0])]}),makeQuery(id+"F5.opExtrude","SWEPT_FACE",FACE,{"disambiguationData":[OSD([subQ0]),TDD([makeQuery(id+"F0.imprint","IMPRINT",EDGE,{"disambiguationData":[TD([[makeQuery(id+"F0.imprint","INTERSECT",VERTEX,{"disambiguationData":[OD(1.0)],"derivedFrom":[sQuery(id+"F0.wireOp",EDGE,"E1.0"),subQ0]}),1.0]])],"derivedFrom":subQ0})])]})]}),makeQuery(id+"F7.opExtrude","SWEPT_FACE",FACE,{"disambiguationData":[OSD([sQuery(id+"F6.wireOp",EDGE,"E29")])]})]});}
            var Q43;
            {var subQ0=sQuery(id+"F0.wireOp",EDGE,"E7.bottom");Q43=makeQuery(id+"F7.boolean.opBoolean","INTERSECT",EDGE,{"derivedFrom":[makeQuery(id+"F5.boolean.opBoolean","MERGE",FACE,{"derivedFrom":[makeQuery(id+"F3.opExtrude","SWEPT_FACE",FACE,{"disambiguationData":[OSD([subQ0]),TDD([makeQuery(id+"F0.imprint","IMPRINT",EDGE,{"disambiguationData":[TD([[makeQuery(id+"F0.imprint","INTERSECT",VERTEX,{"disambiguationData":[OD(0.0)],"derivedFrom":[sQuery(id+"F0.wireOp",EDGE,"E1.0"),subQ0]}),-1.0]])],"derivedFrom":subQ0})])]}),makeQuery(id+"F5.opExtrude","SWEPT_FACE",FACE,{"disambiguationData":[OSD([subQ0])]})]}),makeQuery(id+"F7.opExtrude","SWEPT_FACE",FACE,{"disambiguationData":[OSD([sQuery(id+"F6.wireOp",EDGE,"E30")])]})]});}
            var Q44;
            {var subQ0=sQuery(id+"F0.wireOp",EDGE,"E3.right");Q44=makeQuery(id+"F7.boolean.opBoolean","INTERSECT",EDGE,{"derivedFrom":[makeQuery(id+"F5.boolean.opBoolean","MERGE",FACE,{"derivedFrom":[makeQuery(id+"F3.opExtrude","SWEPT_FACE",FACE,{"disambiguationData":[OSD([subQ0])]}),makeQuery(id+"F5.opExtrude","SWEPT_FACE",FACE,{"disambiguationData":[OSD([subQ0]),TDD([makeQuery(id+"F0.imprint","IMPRINT",EDGE,{"disambiguationData":[TD([[makeQuery(id+"F0.imprint","INTERSECT",VERTEX,{"disambiguationData":[OD(1.0)],"derivedFrom":[sQuery(id+"F0.wireOp",EDGE,"E1.0"),subQ0]}),1.0]])],"derivedFrom":subQ0})])]})]}),makeQuery(id+"F7.opExtrude","SWEPT_FACE",FACE,{"disambiguationData":[OSD([sQuery(id+"F6.wireOp",EDGE,"E29")])]})]});}
            var Q45;
            {var subQ0=sQuery(id+"F0.wireOp",EDGE,"E7.top");Q45=makeQuery(id+"F7.boolean.opBoolean","INTERSECT",EDGE,{"derivedFrom":[makeQuery(id+"F3.opExtrude","SWEPT_FACE",FACE,{"disambiguationData":[OSD([subQ0]),TDD([makeQuery(id+"F0.imprint","IMPRINT",EDGE,{"disambiguationData":[TD([[makeQuery(id+"F0.imprint","INTERSECT",VERTEX,{"disambiguationData":[OD(0.0)],"derivedFrom":[sQuery(id+"F0.wireOp",EDGE,"E1.0"),subQ0]}),-1.0]])],"derivedFrom":subQ0})])]}),makeQuery(id+"F7.opExtrude","SWEPT_FACE",FACE,{"disambiguationData":[OSD([sQuery(id+"F6.wireOp",EDGE,"E30")])]})]});}
            var Q46;
            {var subQ0=sQuery(id+"F0.wireOp",EDGE,"E8.right");Q46=makeQuery(id+"F7.boolean.opBoolean","INTERSECT",EDGE,{"derivedFrom":[makeQuery(id+"F5.boolean.opBoolean","MERGE",FACE,{"derivedFrom":[makeQuery(id+"F3.opExtrude","SWEPT_FACE",FACE,{"disambiguationData":[OSD([subQ0])]}),makeQuery(id+"F5.opExtrude","SWEPT_FACE",FACE,{"disambiguationData":[OSD([subQ0]),TDD([makeQuery(id+"F0.imprint","IMPRINT",EDGE,{"disambiguationData":[TD([[makeQuery(id+"F0.imprint","INTERSECT",VERTEX,{"disambiguationData":[OD(0.0)],"derivedFrom":[sQuery(id+"F0.wireOp",EDGE,"E1.0"),subQ0]}),-1.0]])],"derivedFrom":subQ0})])]})]}),makeQuery(id+"F7.opExtrude","SWEPT_FACE",FACE,{"disambiguationData":[OSD([sQuery(id+"F6.wireOp",EDGE,"E25")])]})]});}
            var Q47;
            Q47=makeQuery(id+"F7.boolean.opBoolean","INTERSECT",EDGE,{"derivedFrom":[makeQuery(id+"F3.opExtrude","SWEPT_FACE",FACE,{"disambiguationData":[OSD([sQuery(id+"F0.wireOp",EDGE,"E8.left")])]}),makeQuery(id+"F7.opExtrude","SWEPT_FACE",FACE,{"disambiguationData":[OSD([sQuery(id+"F6.wireOp",EDGE,"E25")])]})]});
            var Q48;
            Q48=makeQuery(id+"F5.boolean.opBoolean","COPY",EDGE,{"derivedFrom":makeQuery(id+"F5.opExtrude","SWEPT_EDGE",EDGE,{"disambiguationData":[OSD([sQuery(id+"F0.wireOp",EDGE,"E1.0"),sQuery(id+"F0.wireOp",EDGE,"E6.bottom")])]})});
            var Q49;
            Q49=makeQuery(id+"F5.boolean.opBoolean","COPY",EDGE,{"derivedFrom":makeQuery(id+"F5.opExtrude","SWEPT_EDGE",EDGE,{"disambiguationData":[OSD([sQuery(id+"F0.wireOp",EDGE,"E1.0"),sQuery(id+"F0.wireOp",EDGE,"E6.top")])]})});
            var Q50;
            {var subQ0=sQuery(id+"F0.wireOp",EDGE,"E2.left");var subQ1=sQuery(id+"F0.wireOp",EDGE,"E1.0");Q50=makeQuery(id+"F5.boolean.opBoolean","COPY",EDGE,{"derivedFrom":makeQuery(id+"F5.opExtrude","SWEPT_EDGE",EDGE,{"disambiguationData":[OSD([subQ1,subQ0]),TDD([makeQuery(id+"F0.imprint","INTERSECT",VERTEX,{"disambiguationData":[OD(1.0)],"derivedFrom":[subQ1,subQ0]})])]})});}
            fillet(context, id + "F8", {"entities" : qUnion([Q0, Q1, Q2, Q3, Q4, Q5, Q6, Q7, Q8, Q9, Q10, Q11, Q12, Q13, Q14, Q15, Q16, Q17, Q18, Q19, Q20, Q21, Q22, Q23, Q24, Q25, Q26, Q27, Q28, Q29, Q30, Q31, Q32, Q33, Q34, Q35, Q36, Q37, Q38, Q39, Q40, Q41, Q42, Q43, Q44, Q45, Q46, Q47, Q48, Q49, Q50]), "radius" : 1 * mm, "tangentPropagation" : true, "allowEdgeOverflow" : false});
        }
        {
            var Q0;
            {var subQ0=sQuery(id+"F6.wireOp",EDGE,"E31");var subQ1=sQuery(id+"F6.wireOp",EDGE,"E13");var subQ2=makeQuery(id+"F6.imprint","INTERSECT",VERTEX,{"disambiguationData":[OD(0.0)],"derivedFrom":[subQ1,subQ0]});Q0=makeQuery(id+"F6.imprint","IMPRINT",FACE,{"disambiguationData":[TD([[makeQuery(id+"F6.imprint","IMPRINT",EDGE,{"disambiguationData":[TD([[subQ2,-1.0]])],"derivedFrom":subQ1}),-1.0]])]});}
            var Q1;
            {var subQ0=sQuery(id+"F6.wireOp",EDGE,"E31");var subQ1=sQuery(id+"F6.wireOp",EDGE,"E13");var subQ2=makeQuery(id+"F6.imprint","INTERSECT",VERTEX,{"disambiguationData":[OD(0.0)],"derivedFrom":[subQ1,subQ0]});Q1=makeQuery(id+"F6.imprint","IMPRINT",FACE,{"disambiguationData":[TD([[makeQuery(id+"F6.imprint","IMPRINT",EDGE,{"disambiguationData":[TD([[subQ2,-1.0]])],"derivedFrom":subQ1}),1.0]])]});}
            var Q2;
            {var subQ0=sQuery(id+"F6.wireOp",EDGE,"E32");var subQ1=sQuery(id+"F6.wireOp",EDGE,"E13");var subQ2=makeQuery(id+"F6.imprint","INTERSECT",VERTEX,{"disambiguationData":[OD(0.0)],"derivedFrom":[subQ1,subQ0]});Q2=makeQuery(id+"F6.imprint","IMPRINT",FACE,{"disambiguationData":[TD([[makeQuery(id+"F6.imprint","IMPRINT",EDGE,{"disambiguationData":[TD([[subQ2,-1.0]])],"derivedFrom":subQ1}),-1.0]])]});}
            var Q3;
            {var subQ0=sQuery(id+"F6.wireOp",EDGE,"E32");var subQ1=sQuery(id+"F6.wireOp",EDGE,"E13");var subQ2=makeQuery(id+"F6.imprint","INTERSECT",VERTEX,{"disambiguationData":[OD(0.0)],"derivedFrom":[subQ1,subQ0]});Q3=makeQuery(id+"F6.imprint","IMPRINT",FACE,{"disambiguationData":[TD([[makeQuery(id+"F6.imprint","IMPRINT",EDGE,{"disambiguationData":[TD([[subQ2,-1.0]])],"derivedFrom":subQ1}),1.0]])]});}
            var Q4;
            {var subQ0=sQuery(id+"F6.wireOp",EDGE,"E33");var subQ1=sQuery(id+"F6.wireOp",EDGE,"E13");var subQ2=makeQuery(id+"F6.imprint","INTERSECT",VERTEX,{"disambiguationData":[OD(0.0)],"derivedFrom":[subQ1,subQ0]});Q4=makeQuery(id+"F6.imprint","IMPRINT",FACE,{"disambiguationData":[TD([[makeQuery(id+"F6.imprint","IMPRINT",EDGE,{"disambiguationData":[TD([[subQ2,-1.0]])],"derivedFrom":subQ1}),1.0]])]});}
            var Q5;
            {var subQ0=sQuery(id+"F6.wireOp",EDGE,"E33");var subQ1=sQuery(id+"F6.wireOp",EDGE,"E13");var subQ2=makeQuery(id+"F6.imprint","INTERSECT",VERTEX,{"disambiguationData":[OD(0.0)],"derivedFrom":[subQ1,subQ0]});Q5=makeQuery(id+"F6.imprint","IMPRINT",FACE,{"disambiguationData":[TD([[makeQuery(id+"F6.imprint","IMPRINT",EDGE,{"disambiguationData":[TD([[subQ2,-1.0]])],"derivedFrom":subQ1}),-1.0]])]});}
            var Q6;
            {var subQ0=sQuery(id+"F6.wireOp",EDGE,"E34");var subQ1=sQuery(id+"F6.wireOp",EDGE,"E13");var subQ2=makeQuery(id+"F6.imprint","INTERSECT",VERTEX,{"disambiguationData":[OD(0.0)],"derivedFrom":[subQ1,subQ0]});Q6=makeQuery(id+"F6.imprint","IMPRINT",FACE,{"disambiguationData":[TD([[makeQuery(id+"F6.imprint","IMPRINT",EDGE,{"disambiguationData":[TD([[subQ2,-1.0]])],"derivedFrom":subQ1}),1.0]])]});}
            var Q7;
            {var subQ0=sQuery(id+"F6.wireOp",EDGE,"E34");var subQ1=sQuery(id+"F6.wireOp",EDGE,"E13");var subQ2=makeQuery(id+"F6.imprint","INTERSECT",VERTEX,{"disambiguationData":[OD(0.0)],"derivedFrom":[subQ1,subQ0]});Q7=makeQuery(id+"F6.imprint","IMPRINT",FACE,{"disambiguationData":[TD([[makeQuery(id+"F6.imprint","IMPRINT",EDGE,{"disambiguationData":[TD([[subQ2,-1.0]])],"derivedFrom":subQ1}),-1.0]])]});}
            var Q8;
            {var subQ1=sQuery(id+"F6.wireOp",EDGE,"E36.bottom");Q8=makeQuery(id+"F6.imprint","IMPRINT",FACE,{"disambiguationData":[TD([[makeQuery(id+"F6.imprint","IMPRINT",EDGE,{"derivedFrom":subQ1}),-1.0]])]});}
            var Q9;
            {var subQ0=sQuery(id+"F6.wireOp",EDGE,"E36.top");var subQ1=sQuery(id+"F6.wireOp",EDGE,"E13");var subQ2=makeQuery(id+"F6.imprint","INTERSECT",VERTEX,{"derivedFrom":[subQ1,subQ0]});Q9=makeQuery(id+"F6.imprint","IMPRINT",FACE,{"disambiguationData":[TD([[makeQuery(id+"F6.imprint","IMPRINT",EDGE,{"disambiguationData":[TD([[subQ2,-1.0]])],"derivedFrom":subQ1}),1.0]])]});}
            var Q10;
            {var subQ0=sQuery(id+"F6.wireOp",EDGE,"E35");var subQ1=sQuery(id+"F6.wireOp",EDGE,"E13");var subQ2=makeQuery(id+"F6.imprint","INTERSECT",VERTEX,{"disambiguationData":[OD(0.0)],"derivedFrom":[subQ1,subQ0]});Q10=makeQuery(id+"F6.imprint","IMPRINT",FACE,{"disambiguationData":[TD([[makeQuery(id+"F6.imprint","IMPRINT",EDGE,{"disambiguationData":[TD([[subQ2,-1.0]])],"derivedFrom":subQ1}),-1.0]])]});}
            var Q11;
            {var subQ0=sQuery(id+"F6.wireOp",EDGE,"E35");var subQ1=sQuery(id+"F6.wireOp",EDGE,"E13");var subQ2=makeQuery(id+"F6.imprint","INTERSECT",VERTEX,{"disambiguationData":[OD(0.0)],"derivedFrom":[subQ1,subQ0]});Q11=makeQuery(id+"F6.imprint","IMPRINT",FACE,{"disambiguationData":[TD([[makeQuery(id+"F6.imprint","IMPRINT",EDGE,{"disambiguationData":[TD([[subQ2,-1.0]])],"derivedFrom":subQ1}),1.0]])]});}
            extrude(context, id + "F9", {"entities" : qUnion([Q0, Q1, Q2, Q3, Q4, Q5, Q6, Q7, Q8, Q9, Q10, Q11]), "operationType" : NewBodyOperationType.ADD, "depth" : 11 * mm, "offsetDistance" : 25 * mm, "hasDraft" : true, "draftAngle" : .9 * degree, "draftPullDirection" : true});
        }
        {
            var Q0;
            Q0=makeQuery(id+"F9.opExtrude","CAP_EDGE",EDGE,{"disambiguationData":[OSD([sQuery(id+"F6.wireOp",EDGE,"E35")])],"isStart":false});
            var Q1;
            Q1=makeQuery(id+"F9.opExtrude","CAP_FACE",FACE,{"disambiguationData":[OSD([sQuery(id+"F6.wireOp",EDGE,"E31")])],"isStart":false});
            var Q2;
            Q2=makeQuery(id+"F9.opExtrude","CAP_FACE",FACE,{"disambiguationData":[OSD([sQuery(id+"F6.wireOp",EDGE,"E32")])],"isStart":false});
            var Q3;
            Q3=makeQuery(id+"F9.opExtrude","CAP_FACE",FACE,{"disambiguationData":[OSD([sQuery(id+"F6.wireOp",EDGE,"E33")])],"isStart":false});
            var Q4;
            Q4=makeQuery(id+"F9.opExtrude","CAP_FACE",FACE,{"disambiguationData":[OSD([sQuery(id+"F6.wireOp",EDGE,"E34")])],"isStart":false});
            var Q5;
            Q5=makeQuery(id+"F9.opExtrude","CAP_EDGE",EDGE,{"disambiguationData":[OSD([sQuery(id+"F6.wireOp",EDGE,"E36.left")])],"isStart":false});
            var Q6;
            Q6=makeQuery(id+"F9.opExtrude","CAP_EDGE",EDGE,{"disambiguationData":[OSD([sQuery(id+"F6.wireOp",EDGE,"E36.right")])],"isStart":false});
            var Q7;
            Q7=makeQuery(id+"F9.opExtrude","CAP_EDGE",EDGE,{"disambiguationData":[OSD([sQuery(id+"F6.wireOp",EDGE,"E36.bottom")])],"isStart":false});
            var Q8;
            Q8=makeQuery(id+"F9.opExtrude","CAP_EDGE",EDGE,{"disambiguationData":[OSD([sQuery(id+"F6.wireOp",EDGE,"E36.top")])],"isStart":false});
            fillet(context, id + "F10", {"entities" : qUnion([Q0, Q1, Q2, Q3, Q4, Q5, Q6, Q7, Q8]), "radius" : .45 * mm, "tangentPropagation" : true, "allowEdgeOverflow" : false});
        }
        {
            var Q0;
            {var subQ0=sQuery(id+"F6.wireOp",EDGE,"E35");var subQ1=sQuery(id+"F6.wireOp",EDGE,"E13");var subQ2=makeQuery(id+"F6.imprint","INTERSECT",VERTEX,{"disambiguationData":[OD(0.0)],"derivedFrom":[subQ1,subQ0]});Q0=makeQuery(id+"F6.imprint","IMPRINT",FACE,{"disambiguationData":[TD([[makeQuery(id+"F6.imprint","IMPRINT",EDGE,{"disambiguationData":[TD([[subQ2,-1.0]])],"derivedFrom":subQ1}),-1.0]])]});}
            var Q1;
            {var subQ0=sQuery(id+"F6.wireOp",EDGE,"E35");var subQ1=sQuery(id+"F6.wireOp",EDGE,"E13");var subQ2=makeQuery(id+"F6.imprint","INTERSECT",VERTEX,{"disambiguationData":[OD(0.0)],"derivedFrom":[subQ1,subQ0]});Q1=makeQuery(id+"F6.imprint","IMPRINT",FACE,{"disambiguationData":[TD([[makeQuery(id+"F6.imprint","IMPRINT",EDGE,{"disambiguationData":[TD([[subQ2,-1.0]])],"derivedFrom":subQ1}),1.0]])]});}
            var Q2;
            {var subQ1=sQuery(id+"F6.wireOp",EDGE,"E36.bottom");Q2=makeQuery(id+"F6.imprint","IMPRINT",FACE,{"disambiguationData":[TD([[makeQuery(id+"F6.imprint","IMPRINT",EDGE,{"derivedFrom":subQ1}),-1.0]])]});}
            var Q3;
            {var subQ0=sQuery(id+"F6.wireOp",EDGE,"E36.top");var subQ1=sQuery(id+"F6.wireOp",EDGE,"E13");var subQ2=makeQuery(id+"F6.imprint","INTERSECT",VERTEX,{"derivedFrom":[subQ1,subQ0]});Q3=makeQuery(id+"F6.imprint","IMPRINT",FACE,{"disambiguationData":[TD([[makeQuery(id+"F6.imprint","IMPRINT",EDGE,{"disambiguationData":[TD([[subQ2,-1.0]])],"derivedFrom":subQ1}),1.0]])]});}
            var Q4;
            {var subQ0=sQuery(id+"F6.wireOp",EDGE,"E34");var subQ1=sQuery(id+"F6.wireOp",EDGE,"E13");var subQ2=makeQuery(id+"F6.imprint","INTERSECT",VERTEX,{"disambiguationData":[OD(0.0)],"derivedFrom":[subQ1,subQ0]});Q4=makeQuery(id+"F6.imprint","IMPRINT",FACE,{"disambiguationData":[TD([[makeQuery(id+"F6.imprint","IMPRINT",EDGE,{"disambiguationData":[TD([[subQ2,-1.0]])],"derivedFrom":subQ1}),1.0]])]});}
            var Q5;
            {var subQ0=sQuery(id+"F6.wireOp",EDGE,"E34");var subQ1=sQuery(id+"F6.wireOp",EDGE,"E13");var subQ2=makeQuery(id+"F6.imprint","INTERSECT",VERTEX,{"disambiguationData":[OD(0.0)],"derivedFrom":[subQ1,subQ0]});Q5=makeQuery(id+"F6.imprint","IMPRINT",FACE,{"disambiguationData":[TD([[makeQuery(id+"F6.imprint","IMPRINT",EDGE,{"disambiguationData":[TD([[subQ2,-1.0]])],"derivedFrom":subQ1}),-1.0]])]});}
            var Q6;
            {var subQ0=sQuery(id+"F6.wireOp",EDGE,"E33");var subQ1=sQuery(id+"F6.wireOp",EDGE,"E13");var subQ2=makeQuery(id+"F6.imprint","INTERSECT",VERTEX,{"disambiguationData":[OD(0.0)],"derivedFrom":[subQ1,subQ0]});Q6=makeQuery(id+"F6.imprint","IMPRINT",FACE,{"disambiguationData":[TD([[makeQuery(id+"F6.imprint","IMPRINT",EDGE,{"disambiguationData":[TD([[subQ2,-1.0]])],"derivedFrom":subQ1}),1.0]])]});}
            var Q7;
            {var subQ0=sQuery(id+"F6.wireOp",EDGE,"E33");var subQ1=sQuery(id+"F6.wireOp",EDGE,"E13");var subQ2=makeQuery(id+"F6.imprint","INTERSECT",VERTEX,{"disambiguationData":[OD(0.0)],"derivedFrom":[subQ1,subQ0]});Q7=makeQuery(id+"F6.imprint","IMPRINT",FACE,{"disambiguationData":[TD([[makeQuery(id+"F6.imprint","IMPRINT",EDGE,{"disambiguationData":[TD([[subQ2,-1.0]])],"derivedFrom":subQ1}),-1.0]])]});}
            var Q8;
            {var subQ0=sQuery(id+"F6.wireOp",EDGE,"E32");var subQ1=sQuery(id+"F6.wireOp",EDGE,"E13");var subQ2=makeQuery(id+"F6.imprint","INTERSECT",VERTEX,{"disambiguationData":[OD(0.0)],"derivedFrom":[subQ1,subQ0]});Q8=makeQuery(id+"F6.imprint","IMPRINT",FACE,{"disambiguationData":[TD([[makeQuery(id+"F6.imprint","IMPRINT",EDGE,{"disambiguationData":[TD([[subQ2,-1.0]])],"derivedFrom":subQ1}),1.0]])]});}
            var Q9;
            {var subQ0=sQuery(id+"F6.wireOp",EDGE,"E32");var subQ1=sQuery(id+"F6.wireOp",EDGE,"E13");var subQ2=makeQuery(id+"F6.imprint","INTERSECT",VERTEX,{"disambiguationData":[OD(0.0)],"derivedFrom":[subQ1,subQ0]});Q9=makeQuery(id+"F6.imprint","IMPRINT",FACE,{"disambiguationData":[TD([[makeQuery(id+"F6.imprint","IMPRINT",EDGE,{"disambiguationData":[TD([[subQ2,-1.0]])],"derivedFrom":subQ1}),-1.0]])]});}
            var Q10;
            {var subQ0=sQuery(id+"F6.wireOp",EDGE,"E31");var subQ1=sQuery(id+"F6.wireOp",EDGE,"E13");var subQ2=makeQuery(id+"F6.imprint","INTERSECT",VERTEX,{"disambiguationData":[OD(0.0)],"derivedFrom":[subQ1,subQ0]});Q10=makeQuery(id+"F6.imprint","IMPRINT",FACE,{"disambiguationData":[TD([[makeQuery(id+"F6.imprint","IMPRINT",EDGE,{"disambiguationData":[TD([[subQ2,-1.0]])],"derivedFrom":subQ1}),-1.0]])]});}
            var Q11;
            {var subQ0=sQuery(id+"F6.wireOp",EDGE,"E31");var subQ1=sQuery(id+"F6.wireOp",EDGE,"E13");var subQ2=makeQuery(id+"F6.imprint","INTERSECT",VERTEX,{"disambiguationData":[OD(0.0)],"derivedFrom":[subQ1,subQ0]});Q11=makeQuery(id+"F6.imprint","IMPRINT",FACE,{"disambiguationData":[TD([[makeQuery(id+"F6.imprint","IMPRINT",EDGE,{"disambiguationData":[TD([[subQ2,-1.0]])],"derivedFrom":subQ1}),1.0]])]});}
            extrude(context, id + "F11", {"entities" : qUnion([Q0, Q1, Q2, Q3, Q4, Q5, Q6, Q7, Q8, Q9, Q10, Q11]), "operationType" : NewBodyOperationType.REMOVE, "depth" : 3 * mm, "offsetDistance" : 25 * mm});
        }
        {
            var Q0;
            Q0=qCreatedBy(makeId("Top.planeOp"),FACE);
            var sketch = newSketch(context, id + "F12", { "sketchPlane" : qUnion([Q0])});
            skCircle(sketch, "E37", {"center": v(0, 0) * mm, "radius": 17.33 * mm});
            skSolve(sketch);
        }
        {
            var Q0;
            Q0=qSketchRegion(id+"F12",true);
            extrude(context, id + "F13", {"entities" : qUnion([Q0]), "operationType" : NewBodyOperationType.REMOVE, "depth" : 1 * mm, "offsetDistance" : 25 * mm});
        }
    });
